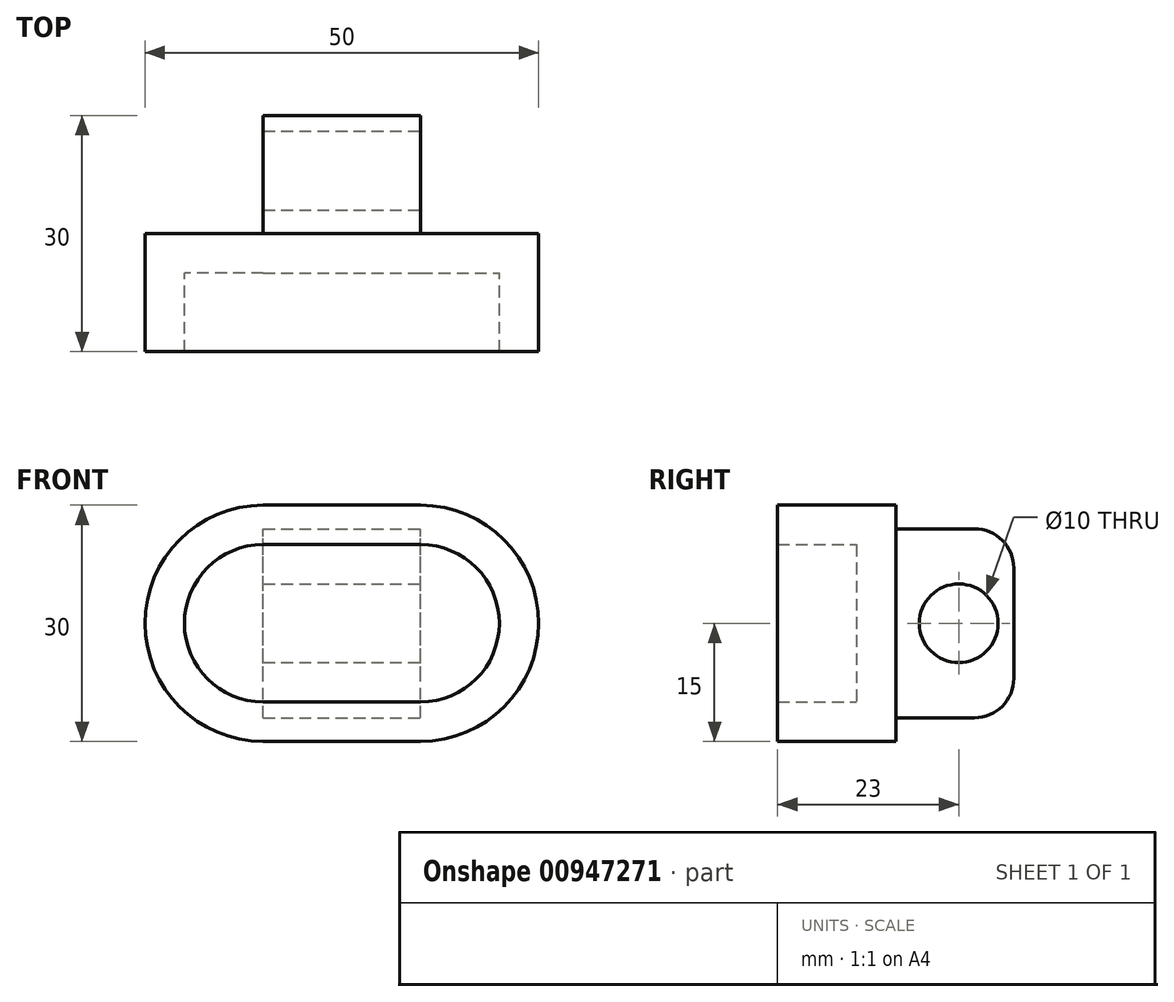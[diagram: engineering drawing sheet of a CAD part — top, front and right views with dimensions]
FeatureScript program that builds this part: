
annotation { "Feature Type Name" : "Feature", "Feature Type Description" : "" }
export const myFeature = defineFeature(function(context is Context, id is Id, definition is map)
    precondition{}
    {
        {
            var Q0;
            Q0=qCreatedBy(makeId("Front.planeOp"),FACE);
            var sketch = newSketch(context, id + "F0", { "sketchPlane" : qUnion([Q0])});
            skArc(sketch, "E0", {"start": v(-10, 10) * mm, "mid": v(-20, 0) * mm, "end": v(-10, -10) * mm});
            skArc(sketch, "E1", {"start": v(10, -10) * mm, "mid": v(20, 0) * mm, "end": v(10, 10) * mm});
            skLineSegment(sketch, "E2", {"start": v(-10, 10) * mm, "end": v(10, 10) * mm});
            skLineSegment(sketch, "E3", {"start": v(-10, -10) * mm, "end": v(10, -10) * mm});
            skArc(sketch, "E4", {"start": v(10, -15) * mm, "mid": v(25, 0) * mm, "end": v(10, 15) * mm});
            skLineSegment(sketch, "E5", {"start": v(-10, 15) * mm, "end": v(10, 15) * mm});
            skLineSegment(sketch, "E6", {"start": v(-10, -15) * mm, "end": v(10, -15) * mm});
            skArc(sketch, "E7.trimOffspring", {"start": v(-10, 15) * mm, "mid": v(-25, 0) * mm, "end": v(-10, -15) * mm});
            skSolve(sketch);
        }
        {
            var Q0;
            Q0 = qSketchRegion(id + "F0", true);
            extrude(context, id + "F1", {"entities" : qUnion([Q0]), "depth" : 15 * mm, "offsetDistance" : 25 * mm});
        }
        {
            var Q0;
            Q0=makeQuery(id+"F1.opExtrude","CAP_FACE",FACE,{"disambiguationData":[OSD([sQuery(id+"F0.wireOp",EDGE,"E0"),sQuery(id+"F0.wireOp",EDGE,"E1"),sQuery(id+"F0.wireOp",EDGE,"E2"),sQuery(id+"F0.wireOp",EDGE,"E3"),sQuery(id+"F0.wireOp",EDGE,"E4"),sQuery(id+"F0.wireOp",EDGE,"E5"),sQuery(id+"F0.wireOp",EDGE,"E6"),sQuery(id+"F0.wireOp",EDGE,"E7.trimOffspring")])],"isStart":true});
            var sketch = newSketch(context, id + "F2", { "sketchPlane" : qUnion([Q0])});
            skArc(sketch, "E8.0", {"start": v(10, 10) * mm, "mid": v(20, 0) * mm, "end": v(10, -10) * mm});
            skLineSegment(sketch, "E8.1", {"start": v(10, -10) * mm, "end": v(-10, -10) * mm});
            skArc(sketch, "E8.2", {"start": v(-10, -10) * mm, "mid": v(-20, 0) * mm, "end": v(-10, 10) * mm});
            skLineSegment(sketch, "E8.3", {"start": v(10, 10) * mm, "end": v(-10, 10) * mm});
            skSolve(sketch);
        }
        {
            var Q0;
            Q0 = qSketchRegion(id + "F2", true);
            extrude(context, id + "F3", {"entities" : qUnion([Q0]), "operationType" : NewBodyOperationType.ADD, "oppositeDirection" : true, "depth" : 5 * mm, "offsetDistance" : 25 * mm});
        }
        {
            var Q0;
            Q0=makeQuery(id+"F3.boolean.opBoolean","MERGE",FACE,{"derivedFrom":[makeQuery(id+"F1.opExtrude","CAP_FACE",FACE,{"disambiguationData":[OSD([sQuery(id+"F0.wireOp",EDGE,"E0"),sQuery(id+"F0.wireOp",EDGE,"E1"),sQuery(id+"F0.wireOp",EDGE,"E2"),sQuery(id+"F0.wireOp",EDGE,"E3"),sQuery(id+"F0.wireOp",EDGE,"E4"),sQuery(id+"F0.wireOp",EDGE,"E5"),sQuery(id+"F0.wireOp",EDGE,"E6"),sQuery(id+"F0.wireOp",EDGE,"E7.trimOffspring")])],"isStart":true}),makeQuery(id+"F3.opExtrude","CAP_FACE",FACE,{"disambiguationData":[OSD([sQuery(id+"F2.wireOp",EDGE,"E8.0"),sQuery(id+"F2.wireOp",EDGE,"E8.1"),sQuery(id+"F2.wireOp",EDGE,"E8.2"),sQuery(id+"F2.wireOp",EDGE,"E8.3")])],"isStart":true})]});
            var sketch = newSketch(context, id + "F4", { "sketchPlane" : qUnion([Q0])});
            skLineSegment(sketch, "E9.bottom", {"start": v(10, -12) * mm, "end": v(-10, -12) * mm});
            skLineSegment(sketch, "E9.top", {"start": v(10, 12) * mm, "end": v(-10, 12) * mm});
            skLineSegment(sketch, "E9.left", {"start": v(10, -12) * mm, "end": v(10, 12) * mm});
            skLineSegment(sketch, "E9.right", {"start": v(-10, -12) * mm, "end": v(-10, 12) * mm});
            skSolve(sketch);
        }
        {
            var Q0;
            Q0 = qSketchRegion(id + "F4", true);
            extrude(context, id + "F5", {"entities" : qUnion([Q0]), "operationType" : NewBodyOperationType.ADD, "depth" : 15 * mm, "offsetDistance" : 25 * mm});
        }
        {
            var Q0;
            Q0=makeQuery(id+"F5.opExtrude","CAP_EDGE",EDGE,{"disambiguationData":[OSD([sQuery(id+"F4.wireOp",EDGE,"E9.bottom")])],"isStart":false});
            var Q1;
            Q1=makeQuery(id+"F5.opExtrude","CAP_EDGE",EDGE,{"disambiguationData":[OSD([sQuery(id+"F4.wireOp",EDGE,"E9.top")])],"isStart":false});
            fillet(context, id + "F6", {"entities" : qUnion([Q0, Q1]), "tangentPropagation" : true, "radius" : 5 * mm, "defaultsChanged" : false, "vertexSettings" : [], "allowEdgeOverflow" : false});
        }
        {
            var Q0;
            Q0=makeQuery(id+"F5.opExtrude","SWEPT_FACE",FACE,{"disambiguationData":[OSD([sQuery(id+"F4.wireOp",EDGE,"E9.right")])]});
            var sketch = newSketch(context, id + "F7", { "sketchPlane" : qUnion([Q0])});
            skCircle(sketch, "E10", {"center": v(8, 0) * mm, "radius": 5 * mm});
            skSolve(sketch);
        }
        {
            var Q0;
            Q0 = qSketchRegion(id + "F7", true);
            extrude(context, id + "F8", {"entities" : qUnion([Q0]), "operationType" : NewBodyOperationType.REMOVE, "oppositeDirection" : true, "depth" : 25 * mm, "offsetDistance" : 25 * mm});
        }
    });
